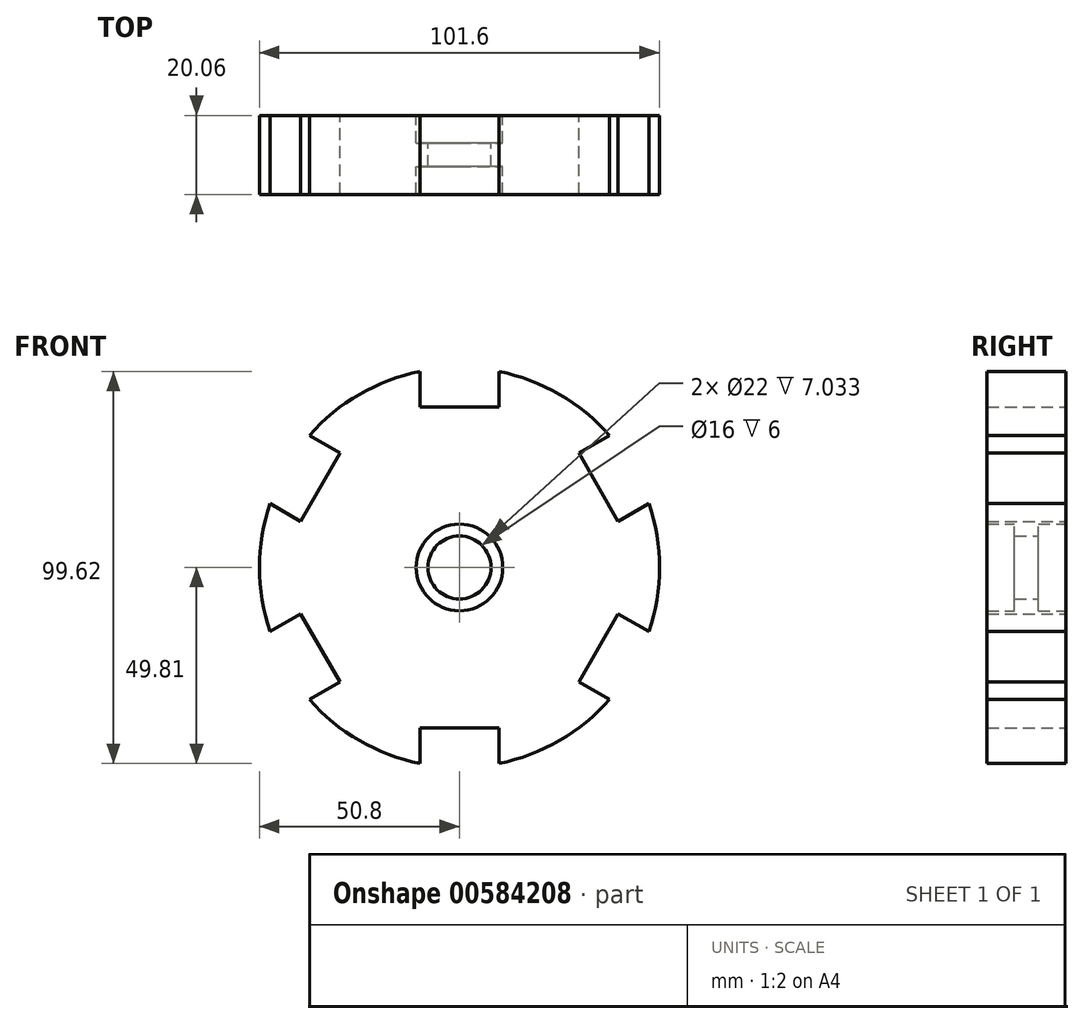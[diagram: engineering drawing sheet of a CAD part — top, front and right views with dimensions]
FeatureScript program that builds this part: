
annotation { "Feature Type Name" : "Feature", "Feature Type Description" : "" }
export const myFeature = defineFeature(function(context is Context, id is Id, definition is map)
    precondition{}
    {
        {
            var Q0;
            Q0=qCreatedBy(makeId("Front.planeOp"),FACE);
            var sketch = newSketch(context, id + "F0", { "sketchPlane" : qUnion([Q0])});
            skCircle(sketch, "E0", {"center": v(0, 0) * mm, "radius": 50.8 * mm});
            skLineSegment(sketch, "E1", {"start": v(0, 0) * mm, "end": v(0, 50.8) * mm, "construction": true});
            skLineSegment(sketch, "E2", {"start": v(0, 0) * mm, "end": v(44, 25.4) * mm, "construction": true});
            skLineSegment(sketch, "E3", {"start": v(0, 0) * mm, "end": v(44, -25.4) * mm, "construction": true});
            skLineSegment(sketch, "E4", {"start": v(0, 0) * mm, "end": v(0, -50.8) * mm, "construction": true});
            skLineSegment(sketch, "E5", {"start": v(0, 0) * mm, "end": v(-44, -25.4) * mm, "construction": true});
            skLineSegment(sketch, "E6", {"start": v(0, 0) * mm, "end": v(-44, 25.4) * mm, "construction": true});
            skLineSegment(sketch, "E7", {"start": v(-10, 50.8) * mm, "end": v(10, 50.8) * mm});
            skLineSegment(sketch, "E8", {"start": v(-10, 50.8) * mm, "end": v(-10, 40.8) * mm});
            skLineSegment(sketch, "E9", {"start": v(-10, 40.8) * mm, "end": v(10, 40.8) * mm});
            skLineSegment(sketch, "E10", {"start": v(10, 40.8) * mm, "end": v(10, 50.8) * mm});
            skCircle(sketch, "E11", {"center": v(0, 0) * mm, "radius": 11 * mm});
            skLineSegment(sketch, "E12.1.0", {"start": v(-49, 16.74) * mm, "end": v(-40.33, 11.74) * mm});
            skLineSegment(sketch, "E12.1.1", {"start": v(-40.33, 11.74) * mm, "end": v(-30.33, 29.06) * mm});
            skLineSegment(sketch, "E12.1.2", {"start": v(-30.33, 29.06) * mm, "end": v(-39, 34.06) * mm});
            skLineSegment(sketch, "E12.2.0", {"start": v(-39, -34.06) * mm, "end": v(-30.33, -29.06) * mm});
            skLineSegment(sketch, "E12.2.1", {"start": v(-30.33, -29.06) * mm, "end": v(-40.33, -11.74) * mm});
            skLineSegment(sketch, "E12.2.2", {"start": v(-40.33, -11.74) * mm, "end": v(-49, -16.74) * mm});
            skLineSegment(sketch, "E13.2.3.0", {"start": v(10, -50.8) * mm, "end": v(10, -40.8) * mm});
            skLineSegment(sketch, "E13.3.3.0", {"start": v(10, -40.8) * mm, "end": v(-10, -40.8) * mm});
            skLineSegment(sketch, "E13.6.3.0", {"start": v(-10, -40.8) * mm, "end": v(-10, -50.8) * mm});
            skLineSegment(sketch, "E13.2.4.0", {"start": v(49, -16.74) * mm, "end": v(40.33, -11.74) * mm});
            skLineSegment(sketch, "E13.3.4.0", {"start": v(40.33, -11.74) * mm, "end": v(30.33, -29.06) * mm});
            skLineSegment(sketch, "E13.6.4.0", {"start": v(30.33, -29.06) * mm, "end": v(39, -34.06) * mm});
            skLineSegment(sketch, "E13.2.5.0", {"start": v(39, 34.06) * mm, "end": v(30.33, 29.06) * mm});
            skLineSegment(sketch, "E13.3.5.0", {"start": v(30.33, 29.06) * mm, "end": v(40.33, 11.74) * mm});
            skLineSegment(sketch, "E13.6.5.0", {"start": v(40.33, 11.74) * mm, "end": v(49, 16.74) * mm});
            skSolve(sketch);
        }
        {
            var Q0;
            Q0=qCreatedBy(makeId("Front.planeOp"),FACE);
            var sketch = newSketch(context, id + "F1", { "sketchPlane" : qUnion([Q0])});
            skCircle(sketch, "E14", {"center": v(0, 0) * mm, "radius": 11 * mm});
            skCircle(sketch, "E15", {"center": v(0, 0) * mm, "radius": 8 * mm});
            skSolve(sketch);
        }
        {
            var Q0;
            {var subQ23=sQuery(id+"F0.wireOp",EDGE,"E9");Q0=makeQuery(id+"F0.imprint","IMPRINT",FACE,{"disambiguationData":[TD([[makeQuery(id+"F0.imprint","IMPRINT",EDGE,{"derivedFrom":subQ23}),-1.0]])]});}
            extrude(context, id + "F2", {"entities" : qUnion([Q0]), "endBound" : BoundingType.SYMMETRIC, "depth" : 20.07 * mm, "offsetDistance" : 25.4 * mm});
        }
        {
            var Q0;
            Q0 = qSketchRegion(id + "F1", true);
            extrude(context, id + "F3", {"entities" : qUnion([Q0]), "operationType" : NewBodyOperationType.ADD, "endBound" : BoundingType.SYMMETRIC, "depth" : 6 * mm, "offsetDistance" : 25.4 * mm});
        }
    });
